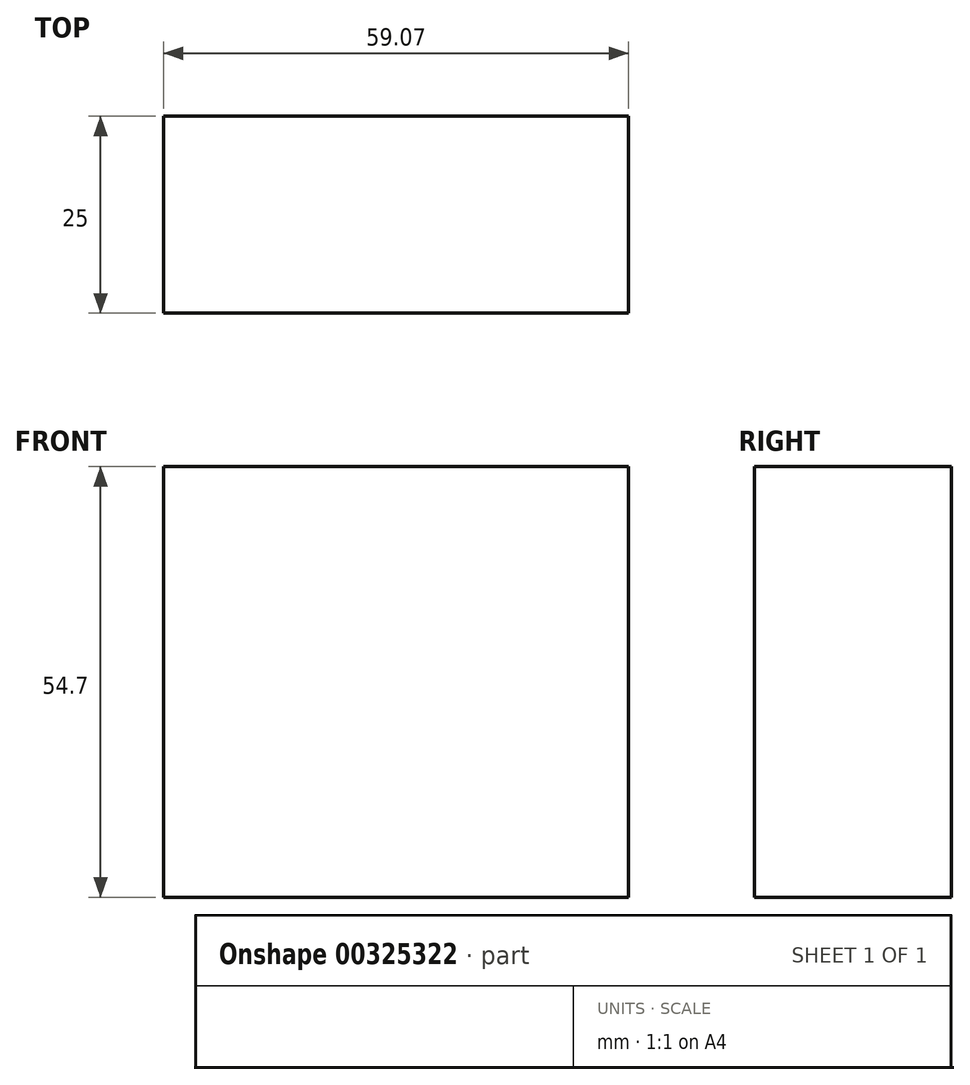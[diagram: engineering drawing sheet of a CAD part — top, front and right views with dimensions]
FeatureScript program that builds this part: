
annotation { "Feature Type Name" : "Feature", "Feature Type Description" : "" }
export const myFeature = defineFeature(function(context is Context, id is Id, definition is map)
    precondition{}
    {
        {
            var Q0;
            Q0=qCreatedBy(makeId("Front.planeOp"),FACE);
            var sketch = newSketch(context, id + "F0", { "sketchPlane" : qUnion([Q0])});
            skLineSegment(sketch, "E0.bottom", {"start": v(-79.84, 30.5) * mm, "end": v(-20.77, 30.5) * mm});
            skLineSegment(sketch, "E0.top", {"start": v(-79.84, 85.2) * mm, "end": v(-20.77, 85.2) * mm});
            skLineSegment(sketch, "E0.left", {"start": v(-79.84, 30.5) * mm, "end": v(-79.84, 85.2) * mm});
            skLineSegment(sketch, "E0.right", {"start": v(-20.77, 30.5) * mm, "end": v(-20.77, 85.2) * mm});
            skPoint(sketch, "E0.middle", {"position": v(-50.3, 57.85) * mm});
            skSolve(sketch);
        }
        {
            var Q0;
            Q0=makeQuery(id+"F0.imprint","IMPRINT",FACE,{"disambiguationData":[TD([[makeQuery(id+"F0.imprint","IMPRINT",EDGE,{"derivedFrom":sQuery(id+"F0.wireOp",EDGE,"E0.bottom")}),1.0]])]});
            extrude(context, id + "F1", {"entities" : qUnion([Q0]), "depth" : 25 * mm});
        }
    });
